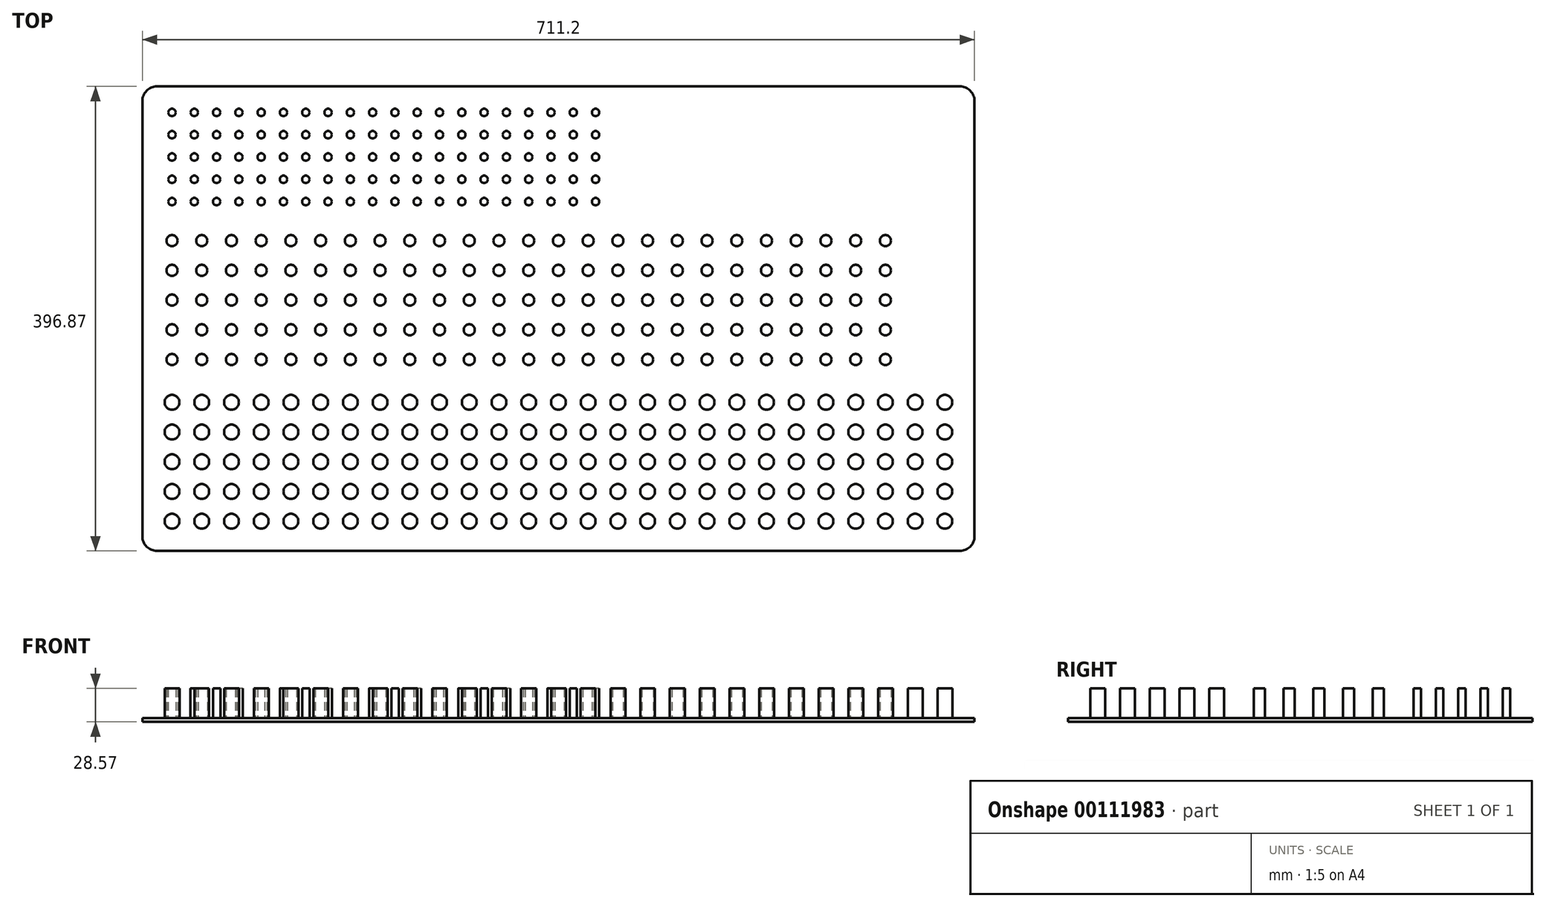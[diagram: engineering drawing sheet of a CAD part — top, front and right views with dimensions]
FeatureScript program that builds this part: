
annotation { "Feature Type Name" : "Feature", "Feature Type Description" : "" }
export const myFeature = defineFeature(function(context is Context, id is Id, definition is map)
    precondition{}
    {
        {
            var Q0;
            Q0=qCreatedBy(makeId("Top.planeOp"),FACE);
            var sketch = newSketch(context, id + "F0", { "sketchPlane" : qUnion([Q0])});
            skCircle(sketch, "E0", {"center": v(0, 97.83) * mm, "radius": 3.17 * mm});
            skCircle(sketch, "E1.0.1.0", {"center": v(0, 116.88) * mm, "radius": 3.17 * mm});
            skCircle(sketch, "E1.0.2.0", {"center": v(0, 135.93) * mm, "radius": 3.17 * mm});
            skCircle(sketch, "E1.0.3.0", {"center": v(0, 154.98) * mm, "radius": 3.17 * mm});
            skCircle(sketch, "E1.0.4.0", {"center": v(0, 174.03) * mm, "radius": 3.17 * mm});
            skCircle(sketch, "E1.1.0.0", {"center": v(19.05, 97.83) * mm, "radius": 3.17 * mm});
            skCircle(sketch, "E1.1.1.0", {"center": v(19.05, 116.88) * mm, "radius": 3.17 * mm});
            skCircle(sketch, "E1.1.2.0", {"center": v(19.05, 135.93) * mm, "radius": 3.17 * mm});
            skCircle(sketch, "E1.1.3.0", {"center": v(19.05, 154.98) * mm, "radius": 3.17 * mm});
            skCircle(sketch, "E1.1.4.0", {"center": v(19.05, 174.03) * mm, "radius": 3.17 * mm});
            skCircle(sketch, "E1.2.0.0", {"center": v(38.1, 97.83) * mm, "radius": 3.17 * mm});
            skCircle(sketch, "E1.2.1.0", {"center": v(38.1, 116.88) * mm, "radius": 3.17 * mm});
            skCircle(sketch, "E1.2.2.0", {"center": v(38.1, 135.93) * mm, "radius": 3.17 * mm});
            skCircle(sketch, "E1.2.3.0", {"center": v(38.1, 154.98) * mm, "radius": 3.17 * mm});
            skCircle(sketch, "E1.2.4.0", {"center": v(38.1, 174.03) * mm, "radius": 3.17 * mm});
            skCircle(sketch, "E1.3.0.0", {"center": v(57.15, 97.83) * mm, "radius": 3.17 * mm});
            skCircle(sketch, "E1.3.1.0", {"center": v(57.15, 116.88) * mm, "radius": 3.17 * mm});
            skCircle(sketch, "E1.3.2.0", {"center": v(57.15, 135.93) * mm, "radius": 3.17 * mm});
            skCircle(sketch, "E1.3.3.0", {"center": v(57.15, 154.98) * mm, "radius": 3.17 * mm});
            skCircle(sketch, "E1.3.4.0", {"center": v(57.15, 174.03) * mm, "radius": 3.17 * mm});
            skCircle(sketch, "E1.4.0.0", {"center": v(76.2, 97.83) * mm, "radius": 3.17 * mm});
            skCircle(sketch, "E1.4.1.0", {"center": v(76.2, 116.88) * mm, "radius": 3.17 * mm});
            skCircle(sketch, "E1.4.2.0", {"center": v(76.2, 135.93) * mm, "radius": 3.17 * mm});
            skCircle(sketch, "E1.4.3.0", {"center": v(76.2, 154.98) * mm, "radius": 3.17 * mm});
            skCircle(sketch, "E1.4.4.0", {"center": v(76.2, 174.03) * mm, "radius": 3.17 * mm});
            skCircle(sketch, "E1.5.0.0", {"center": v(95.25, 97.83) * mm, "radius": 3.17 * mm});
            skCircle(sketch, "E1.5.1.0", {"center": v(95.25, 116.88) * mm, "radius": 3.17 * mm});
            skCircle(sketch, "E1.5.2.0", {"center": v(95.25, 135.93) * mm, "radius": 3.17 * mm});
            skCircle(sketch, "E1.5.3.0", {"center": v(95.25, 154.98) * mm, "radius": 3.17 * mm});
            skCircle(sketch, "E1.5.4.0", {"center": v(95.25, 174.03) * mm, "radius": 3.17 * mm});
            skCircle(sketch, "E1.6.0.0", {"center": v(114.3, 97.83) * mm, "radius": 3.17 * mm});
            skCircle(sketch, "E1.6.1.0", {"center": v(114.3, 116.88) * mm, "radius": 3.17 * mm});
            skCircle(sketch, "E1.6.2.0", {"center": v(114.3, 135.93) * mm, "radius": 3.17 * mm});
            skCircle(sketch, "E1.6.3.0", {"center": v(114.3, 154.98) * mm, "radius": 3.17 * mm});
            skCircle(sketch, "E1.6.4.0", {"center": v(114.3, 174.03) * mm, "radius": 3.17 * mm});
            skCircle(sketch, "E1.7.0.0", {"center": v(133.35, 97.83) * mm, "radius": 3.17 * mm});
            skCircle(sketch, "E1.7.1.0", {"center": v(133.35, 116.88) * mm, "radius": 3.17 * mm});
            skCircle(sketch, "E1.7.2.0", {"center": v(133.35, 135.93) * mm, "radius": 3.17 * mm});
            skCircle(sketch, "E1.7.3.0", {"center": v(133.35, 154.98) * mm, "radius": 3.17 * mm});
            skCircle(sketch, "E1.7.4.0", {"center": v(133.35, 174.03) * mm, "radius": 3.17 * mm});
            skCircle(sketch, "E1.8.0.0", {"center": v(152.4, 97.83) * mm, "radius": 3.17 * mm});
            skCircle(sketch, "E1.8.1.0", {"center": v(152.4, 116.88) * mm, "radius": 3.17 * mm});
            skCircle(sketch, "E1.8.2.0", {"center": v(152.4, 135.93) * mm, "radius": 3.17 * mm});
            skCircle(sketch, "E1.8.3.0", {"center": v(152.4, 154.98) * mm, "radius": 3.17 * mm});
            skCircle(sketch, "E1.8.4.0", {"center": v(152.4, 174.03) * mm, "radius": 3.17 * mm});
            skCircle(sketch, "E1.9.0.0", {"center": v(171.45, 97.83) * mm, "radius": 3.17 * mm});
            skCircle(sketch, "E1.9.1.0", {"center": v(171.45, 116.88) * mm, "radius": 3.17 * mm});
            skCircle(sketch, "E1.9.2.0", {"center": v(171.45, 135.93) * mm, "radius": 3.17 * mm});
            skCircle(sketch, "E1.9.3.0", {"center": v(171.45, 154.98) * mm, "radius": 3.17 * mm});
            skCircle(sketch, "E1.9.4.0", {"center": v(171.45, 174.03) * mm, "radius": 3.17 * mm});
            skCircle(sketch, "E1.10.0.0", {"center": v(190.5, 97.83) * mm, "radius": 3.17 * mm});
            skCircle(sketch, "E1.10.1.0", {"center": v(190.5, 116.88) * mm, "radius": 3.17 * mm});
            skCircle(sketch, "E1.10.2.0", {"center": v(190.5, 135.93) * mm, "radius": 3.17 * mm});
            skCircle(sketch, "E1.10.3.0", {"center": v(190.5, 154.98) * mm, "radius": 3.17 * mm});
            skCircle(sketch, "E1.10.4.0", {"center": v(190.5, 174.03) * mm, "radius": 3.17 * mm});
            skCircle(sketch, "E1.11.0.0", {"center": v(209.55, 97.83) * mm, "radius": 3.17 * mm});
            skCircle(sketch, "E1.11.1.0", {"center": v(209.55, 116.88) * mm, "radius": 3.17 * mm});
            skCircle(sketch, "E1.11.2.0", {"center": v(209.55, 135.93) * mm, "radius": 3.17 * mm});
            skCircle(sketch, "E1.11.3.0", {"center": v(209.55, 154.98) * mm, "radius": 3.17 * mm});
            skCircle(sketch, "E1.11.4.0", {"center": v(209.55, 174.03) * mm, "radius": 3.17 * mm});
            skCircle(sketch, "E1.12.0.0", {"center": v(228.6, 97.83) * mm, "radius": 3.17 * mm});
            skCircle(sketch, "E1.12.1.0", {"center": v(228.6, 116.88) * mm, "radius": 3.17 * mm});
            skCircle(sketch, "E1.12.2.0", {"center": v(228.6, 135.93) * mm, "radius": 3.17 * mm});
            skCircle(sketch, "E1.12.3.0", {"center": v(228.6, 154.98) * mm, "radius": 3.17 * mm});
            skCircle(sketch, "E1.12.4.0", {"center": v(228.6, 174.03) * mm, "radius": 3.17 * mm});
            skCircle(sketch, "E1.13.0.0", {"center": v(247.65, 97.83) * mm, "radius": 3.17 * mm});
            skCircle(sketch, "E1.13.1.0", {"center": v(247.65, 116.88) * mm, "radius": 3.17 * mm});
            skCircle(sketch, "E1.13.2.0", {"center": v(247.65, 135.93) * mm, "radius": 3.17 * mm});
            skCircle(sketch, "E1.13.3.0", {"center": v(247.65, 154.98) * mm, "radius": 3.17 * mm});
            skCircle(sketch, "E1.13.4.0", {"center": v(247.65, 174.03) * mm, "radius": 3.17 * mm});
            skCircle(sketch, "E1.14.0.0", {"center": v(266.7, 97.83) * mm, "radius": 3.17 * mm});
            skCircle(sketch, "E1.14.1.0", {"center": v(266.7, 116.88) * mm, "radius": 3.17 * mm});
            skCircle(sketch, "E1.14.2.0", {"center": v(266.7, 135.93) * mm, "radius": 3.17 * mm});
            skCircle(sketch, "E1.14.3.0", {"center": v(266.7, 154.98) * mm, "radius": 3.17 * mm});
            skCircle(sketch, "E1.14.4.0", {"center": v(266.7, 174.03) * mm, "radius": 3.17 * mm});
            skLineSegment(sketch, "E1.direction1", {"start": v(0, 97.83) * mm, "end": v(19.05, 97.83) * mm, "construction": true});
            skLineSegment(sketch, "E1.direction2", {"start": v(0, 97.83) * mm, "end": v(0, 116.88) * mm, "construction": true});
            skLineSegment(sketch, "E2", {"start": v(0, 174.03) * mm, "end": v(0, -304.85) * mm, "construction": true});
            skCircle(sketch, "E3", {"center": v(0, 64.49) * mm, "radius": 4.76 * mm});
            skCircle(sketch, "E4.0.1.0", {"center": v(0, 39.09) * mm, "radius": 4.76 * mm});
            skCircle(sketch, "E4.0.2.0", {"center": v(0, 13.69) * mm, "radius": 4.76 * mm});
            skCircle(sketch, "E4.0.3.0", {"center": v(0, -11.71) * mm, "radius": 4.76 * mm});
            skCircle(sketch, "E4.0.4.0", {"center": v(0, -37.11) * mm, "radius": 4.76 * mm});
            skCircle(sketch, "E4.1.0.0", {"center": v(25.4, 64.49) * mm, "radius": 4.76 * mm});
            skCircle(sketch, "E4.1.1.0", {"center": v(25.4, 39.09) * mm, "radius": 4.76 * mm});
            skCircle(sketch, "E4.1.2.0", {"center": v(25.4, 13.69) * mm, "radius": 4.76 * mm});
            skCircle(sketch, "E4.1.3.0", {"center": v(25.4, -11.71) * mm, "radius": 4.76 * mm});
            skCircle(sketch, "E4.1.4.0", {"center": v(25.4, -37.11) * mm, "radius": 4.76 * mm});
            skCircle(sketch, "E4.2.0.0", {"center": v(50.8, 64.49) * mm, "radius": 4.76 * mm});
            skCircle(sketch, "E4.2.1.0", {"center": v(50.8, 39.09) * mm, "radius": 4.76 * mm});
            skCircle(sketch, "E4.2.2.0", {"center": v(50.8, 13.69) * mm, "radius": 4.76 * mm});
            skCircle(sketch, "E4.2.3.0", {"center": v(50.8, -11.71) * mm, "radius": 4.76 * mm});
            skCircle(sketch, "E4.2.4.0", {"center": v(50.8, -37.11) * mm, "radius": 4.76 * mm});
            skCircle(sketch, "E4.3.0.0", {"center": v(76.2, 64.49) * mm, "radius": 4.76 * mm});
            skCircle(sketch, "E4.3.1.0", {"center": v(76.2, 39.09) * mm, "radius": 4.76 * mm});
            skCircle(sketch, "E4.3.2.0", {"center": v(76.2, 13.69) * mm, "radius": 4.76 * mm});
            skCircle(sketch, "E4.3.3.0", {"center": v(76.2, -11.71) * mm, "radius": 4.76 * mm});
            skCircle(sketch, "E4.3.4.0", {"center": v(76.2, -37.11) * mm, "radius": 4.76 * mm});
            skCircle(sketch, "E4.4.0.0", {"center": v(101.6, 64.49) * mm, "radius": 4.76 * mm});
            skCircle(sketch, "E4.4.1.0", {"center": v(101.6, 39.09) * mm, "radius": 4.76 * mm});
            skCircle(sketch, "E4.4.2.0", {"center": v(101.6, 13.69) * mm, "radius": 4.76 * mm});
            skCircle(sketch, "E4.4.3.0", {"center": v(101.6, -11.71) * mm, "radius": 4.76 * mm});
            skCircle(sketch, "E4.4.4.0", {"center": v(101.6, -37.11) * mm, "radius": 4.76 * mm});
            skCircle(sketch, "E4.5.0.0", {"center": v(127, 64.49) * mm, "radius": 4.76 * mm});
            skCircle(sketch, "E4.5.1.0", {"center": v(127, 39.09) * mm, "radius": 4.76 * mm});
            skCircle(sketch, "E4.5.2.0", {"center": v(127, 13.69) * mm, "radius": 4.76 * mm});
            skCircle(sketch, "E4.5.3.0", {"center": v(127, -11.71) * mm, "radius": 4.76 * mm});
            skCircle(sketch, "E4.5.4.0", {"center": v(127, -37.11) * mm, "radius": 4.76 * mm});
            skCircle(sketch, "E4.6.0.0", {"center": v(152.4, 64.49) * mm, "radius": 4.76 * mm});
            skCircle(sketch, "E4.6.1.0", {"center": v(152.4, 39.09) * mm, "radius": 4.76 * mm});
            skCircle(sketch, "E4.6.2.0", {"center": v(152.4, 13.69) * mm, "radius": 4.76 * mm});
            skCircle(sketch, "E4.6.3.0", {"center": v(152.4, -11.71) * mm, "radius": 4.76 * mm});
            skCircle(sketch, "E4.6.4.0", {"center": v(152.4, -37.11) * mm, "radius": 4.76 * mm});
            skCircle(sketch, "E4.7.0.0", {"center": v(177.8, 64.49) * mm, "radius": 4.76 * mm});
            skCircle(sketch, "E4.7.1.0", {"center": v(177.8, 39.09) * mm, "radius": 4.76 * mm});
            skCircle(sketch, "E4.7.2.0", {"center": v(177.8, 13.69) * mm, "radius": 4.76 * mm});
            skCircle(sketch, "E4.7.3.0", {"center": v(177.8, -11.71) * mm, "radius": 4.76 * mm});
            skCircle(sketch, "E4.7.4.0", {"center": v(177.8, -37.11) * mm, "radius": 4.76 * mm});
            skCircle(sketch, "E4.8.0.0", {"center": v(203.2, 64.49) * mm, "radius": 4.76 * mm});
            skCircle(sketch, "E4.8.1.0", {"center": v(203.2, 39.09) * mm, "radius": 4.76 * mm});
            skCircle(sketch, "E4.8.2.0", {"center": v(203.2, 13.69) * mm, "radius": 4.76 * mm});
            skCircle(sketch, "E4.8.3.0", {"center": v(203.2, -11.71) * mm, "radius": 4.76 * mm});
            skCircle(sketch, "E4.8.4.0", {"center": v(203.2, -37.11) * mm, "radius": 4.76 * mm});
            skCircle(sketch, "E4.9.0.0", {"center": v(228.6, 64.49) * mm, "radius": 4.76 * mm});
            skCircle(sketch, "E4.9.1.0", {"center": v(228.6, 39.09) * mm, "radius": 4.76 * mm});
            skCircle(sketch, "E4.9.2.0", {"center": v(228.6, 13.69) * mm, "radius": 4.76 * mm});
            skCircle(sketch, "E4.9.3.0", {"center": v(228.6, -11.71) * mm, "radius": 4.76 * mm});
            skCircle(sketch, "E4.9.4.0", {"center": v(228.6, -37.11) * mm, "radius": 4.76 * mm});
            skCircle(sketch, "E4.10.0.0", {"center": v(254, 64.49) * mm, "radius": 4.76 * mm});
            skCircle(sketch, "E4.10.1.0", {"center": v(254, 39.09) * mm, "radius": 4.76 * mm});
            skCircle(sketch, "E4.10.2.0", {"center": v(254, 13.69) * mm, "radius": 4.76 * mm});
            skCircle(sketch, "E4.10.3.0", {"center": v(254, -11.71) * mm, "radius": 4.76 * mm});
            skCircle(sketch, "E4.10.4.0", {"center": v(254, -37.11) * mm, "radius": 4.76 * mm});
            skCircle(sketch, "E4.11.0.0", {"center": v(279.4, 64.49) * mm, "radius": 4.76 * mm});
            skCircle(sketch, "E4.11.1.0", {"center": v(279.4, 39.09) * mm, "radius": 4.76 * mm});
            skCircle(sketch, "E4.11.2.0", {"center": v(279.4, 13.69) * mm, "radius": 4.76 * mm});
            skCircle(sketch, "E4.11.3.0", {"center": v(279.4, -11.71) * mm, "radius": 4.76 * mm});
            skCircle(sketch, "E4.11.4.0", {"center": v(279.4, -37.11) * mm, "radius": 4.76 * mm});
            skCircle(sketch, "E4.12.0.0", {"center": v(304.8, 64.49) * mm, "radius": 4.76 * mm});
            skCircle(sketch, "E4.12.1.0", {"center": v(304.8, 39.09) * mm, "radius": 4.76 * mm});
            skCircle(sketch, "E4.12.2.0", {"center": v(304.8, 13.69) * mm, "radius": 4.76 * mm});
            skCircle(sketch, "E4.12.3.0", {"center": v(304.8, -11.71) * mm, "radius": 4.76 * mm});
            skCircle(sketch, "E4.12.4.0", {"center": v(304.8, -37.11) * mm, "radius": 4.76 * mm});
            skCircle(sketch, "E4.13.0.0", {"center": v(330.2, 64.49) * mm, "radius": 4.76 * mm});
            skCircle(sketch, "E4.13.1.0", {"center": v(330.2, 39.09) * mm, "radius": 4.76 * mm});
            skCircle(sketch, "E4.13.2.0", {"center": v(330.2, 13.69) * mm, "radius": 4.76 * mm});
            skCircle(sketch, "E4.13.3.0", {"center": v(330.2, -11.71) * mm, "radius": 4.76 * mm});
            skCircle(sketch, "E4.13.4.0", {"center": v(330.2, -37.11) * mm, "radius": 4.76 * mm});
            skCircle(sketch, "E4.14.0.0", {"center": v(355.6, 64.49) * mm, "radius": 4.76 * mm});
            skCircle(sketch, "E4.14.1.0", {"center": v(355.6, 39.09) * mm, "radius": 4.76 * mm});
            skCircle(sketch, "E4.14.2.0", {"center": v(355.6, 13.69) * mm, "radius": 4.76 * mm});
            skCircle(sketch, "E4.14.3.0", {"center": v(355.6, -11.71) * mm, "radius": 4.76 * mm});
            skCircle(sketch, "E4.14.4.0", {"center": v(355.6, -37.11) * mm, "radius": 4.76 * mm});
            skCircle(sketch, "E4.15.0.0", {"center": v(381, 64.49) * mm, "radius": 4.76 * mm});
            skCircle(sketch, "E4.15.1.0", {"center": v(381, 39.09) * mm, "radius": 4.76 * mm});
            skCircle(sketch, "E4.15.2.0", {"center": v(381, 13.69) * mm, "radius": 4.76 * mm});
            skCircle(sketch, "E4.15.3.0", {"center": v(381, -11.71) * mm, "radius": 4.76 * mm});
            skCircle(sketch, "E4.15.4.0", {"center": v(381, -37.11) * mm, "radius": 4.76 * mm});
            skCircle(sketch, "E4.16.0.0", {"center": v(406.4, 64.49) * mm, "radius": 4.76 * mm});
            skCircle(sketch, "E4.16.1.0", {"center": v(406.4, 39.09) * mm, "radius": 4.76 * mm});
            skCircle(sketch, "E4.16.2.0", {"center": v(406.4, 13.69) * mm, "radius": 4.76 * mm});
            skCircle(sketch, "E4.16.3.0", {"center": v(406.4, -11.71) * mm, "radius": 4.76 * mm});
            skCircle(sketch, "E4.16.4.0", {"center": v(406.4, -37.11) * mm, "radius": 4.76 * mm});
            skLineSegment(sketch, "E4.direction1", {"start": v(0, 64.49) * mm, "end": v(25.4, 64.49) * mm, "construction": true});
            skLineSegment(sketch, "E4.direction2", {"start": v(0, 64.49) * mm, "end": v(0, 39.09) * mm, "construction": true});
            skCircle(sketch, "E5", {"center": v(0, -73.62) * mm, "radius": 6.35 * mm});
            skCircle(sketch, "E6.0.15.0", {"center": v(285.75, 97.83) * mm, "radius": 3.17 * mm});
            skCircle(sketch, "E6.0.15.1", {"center": v(285.75, 116.88) * mm, "radius": 3.17 * mm});
            skCircle(sketch, "E6.0.15.2", {"center": v(285.75, 135.93) * mm, "radius": 3.17 * mm});
            skCircle(sketch, "E6.0.15.3", {"center": v(285.75, 154.98) * mm, "radius": 3.17 * mm});
            skCircle(sketch, "E6.0.15.4", {"center": v(285.75, 174.03) * mm, "radius": 3.17 * mm});
            skCircle(sketch, "E6.0.16.0", {"center": v(304.8, 97.83) * mm, "radius": 3.17 * mm});
            skCircle(sketch, "E6.0.16.1", {"center": v(304.8, 116.88) * mm, "radius": 3.17 * mm});
            skCircle(sketch, "E6.0.16.2", {"center": v(304.8, 135.93) * mm, "radius": 3.17 * mm});
            skCircle(sketch, "E6.0.16.3", {"center": v(304.8, 154.98) * mm, "radius": 3.17 * mm});
            skCircle(sketch, "E6.0.16.4", {"center": v(304.8, 174.03) * mm, "radius": 3.17 * mm});
            skCircle(sketch, "E6.0.17.0", {"center": v(323.85, 97.83) * mm, "radius": 3.17 * mm});
            skCircle(sketch, "E6.0.17.1", {"center": v(323.85, 116.88) * mm, "radius": 3.17 * mm});
            skCircle(sketch, "E6.0.17.2", {"center": v(323.85, 135.93) * mm, "radius": 3.17 * mm});
            skCircle(sketch, "E6.0.17.3", {"center": v(323.85, 154.98) * mm, "radius": 3.17 * mm});
            skCircle(sketch, "E6.0.17.4", {"center": v(323.85, 174.03) * mm, "radius": 3.17 * mm});
            skCircle(sketch, "E6.0.18.0", {"center": v(342.9, 97.83) * mm, "radius": 3.17 * mm});
            skCircle(sketch, "E6.0.18.1", {"center": v(342.9, 116.88) * mm, "radius": 3.17 * mm});
            skCircle(sketch, "E6.0.18.2", {"center": v(342.9, 135.93) * mm, "radius": 3.17 * mm});
            skCircle(sketch, "E6.0.18.3", {"center": v(342.9, 154.98) * mm, "radius": 3.17 * mm});
            skCircle(sketch, "E6.0.18.4", {"center": v(342.9, 174.03) * mm, "radius": 3.17 * mm});
            skCircle(sketch, "E6.0.19.0", {"center": v(361.95, 97.83) * mm, "radius": 3.17 * mm});
            skCircle(sketch, "E6.0.19.1", {"center": v(361.95, 116.88) * mm, "radius": 3.17 * mm});
            skCircle(sketch, "E6.0.19.2", {"center": v(361.95, 135.93) * mm, "radius": 3.17 * mm});
            skCircle(sketch, "E6.0.19.3", {"center": v(361.95, 154.98) * mm, "radius": 3.17 * mm});
            skCircle(sketch, "E6.0.19.4", {"center": v(361.95, 174.03) * mm, "radius": 3.17 * mm});
            skCircle(sketch, "E7.0.17.0", {"center": v(431.8, 64.49) * mm, "radius": 4.76 * mm});
            skCircle(sketch, "E7.0.17.1", {"center": v(431.8, 39.09) * mm, "radius": 4.76 * mm});
            skCircle(sketch, "E7.0.17.2", {"center": v(431.8, 13.69) * mm, "radius": 4.76 * mm});
            skCircle(sketch, "E7.0.17.3", {"center": v(431.8, -11.71) * mm, "radius": 4.76 * mm});
            skCircle(sketch, "E7.0.17.4", {"center": v(431.8, -37.11) * mm, "radius": 4.76 * mm});
            skCircle(sketch, "E7.0.18.0", {"center": v(457.2, 64.49) * mm, "radius": 4.76 * mm});
            skCircle(sketch, "E7.0.18.1", {"center": v(457.2, 39.09) * mm, "radius": 4.76 * mm});
            skCircle(sketch, "E7.0.18.2", {"center": v(457.2, 13.69) * mm, "radius": 4.76 * mm});
            skCircle(sketch, "E7.0.18.3", {"center": v(457.2, -11.71) * mm, "radius": 4.76 * mm});
            skCircle(sketch, "E7.0.18.4", {"center": v(457.2, -37.11) * mm, "radius": 4.76 * mm});
            skCircle(sketch, "E7.0.19.0", {"center": v(482.6, 64.49) * mm, "radius": 4.76 * mm});
            skCircle(sketch, "E7.0.19.1", {"center": v(482.6, 39.09) * mm, "radius": 4.76 * mm});
            skCircle(sketch, "E7.0.19.2", {"center": v(482.6, 13.69) * mm, "radius": 4.76 * mm});
            skCircle(sketch, "E7.0.19.3", {"center": v(482.6, -11.71) * mm, "radius": 4.76 * mm});
            skCircle(sketch, "E7.0.19.4", {"center": v(482.6, -37.11) * mm, "radius": 4.76 * mm});
            skCircle(sketch, "E7.0.20.0", {"center": v(508, 64.49) * mm, "radius": 4.76 * mm});
            skCircle(sketch, "E7.0.20.1", {"center": v(508, 39.09) * mm, "radius": 4.76 * mm});
            skCircle(sketch, "E7.0.20.2", {"center": v(508, 13.69) * mm, "radius": 4.76 * mm});
            skCircle(sketch, "E7.0.20.3", {"center": v(508, -11.71) * mm, "radius": 4.76 * mm});
            skCircle(sketch, "E7.0.20.4", {"center": v(508, -37.11) * mm, "radius": 4.76 * mm});
            skCircle(sketch, "E7.0.21.0", {"center": v(533.4, 64.49) * mm, "radius": 4.76 * mm});
            skCircle(sketch, "E7.0.21.1", {"center": v(533.4, 39.09) * mm, "radius": 4.76 * mm});
            skCircle(sketch, "E7.0.21.2", {"center": v(533.4, 13.69) * mm, "radius": 4.76 * mm});
            skCircle(sketch, "E7.0.21.3", {"center": v(533.4, -11.71) * mm, "radius": 4.76 * mm});
            skCircle(sketch, "E7.0.21.4", {"center": v(533.4, -37.11) * mm, "radius": 4.76 * mm});
            skCircle(sketch, "E7.0.22.0", {"center": v(558.8, 64.49) * mm, "radius": 4.76 * mm});
            skCircle(sketch, "E7.0.22.1", {"center": v(558.8, 39.09) * mm, "radius": 4.76 * mm});
            skCircle(sketch, "E7.0.22.2", {"center": v(558.8, 13.69) * mm, "radius": 4.76 * mm});
            skCircle(sketch, "E7.0.22.3", {"center": v(558.8, -11.71) * mm, "radius": 4.76 * mm});
            skCircle(sketch, "E7.0.22.4", {"center": v(558.8, -37.11) * mm, "radius": 4.76 * mm});
            skCircle(sketch, "E7.0.23.0", {"center": v(584.2, 64.49) * mm, "radius": 4.76 * mm});
            skCircle(sketch, "E7.0.23.1", {"center": v(584.2, 39.09) * mm, "radius": 4.76 * mm});
            skCircle(sketch, "E7.0.23.2", {"center": v(584.2, 13.69) * mm, "radius": 4.76 * mm});
            skCircle(sketch, "E7.0.23.3", {"center": v(584.2, -11.71) * mm, "radius": 4.76 * mm});
            skCircle(sketch, "E7.0.23.4", {"center": v(584.2, -37.11) * mm, "radius": 4.76 * mm});
            skCircle(sketch, "E7.0.24.0", {"center": v(609.6, 64.49) * mm, "radius": 4.76 * mm});
            skCircle(sketch, "E7.0.24.1", {"center": v(609.6, 39.09) * mm, "radius": 4.76 * mm});
            skCircle(sketch, "E7.0.24.2", {"center": v(609.6, 13.69) * mm, "radius": 4.76 * mm});
            skCircle(sketch, "E7.0.24.3", {"center": v(609.6, -11.71) * mm, "radius": 4.76 * mm});
            skCircle(sketch, "E7.0.24.4", {"center": v(609.6, -37.11) * mm, "radius": 4.76 * mm});
            skCircle(sketch, "E8.0.1.0", {"center": v(0, -99.02) * mm, "radius": 6.35 * mm});
            skCircle(sketch, "E8.0.2.0", {"center": v(0, -124.42) * mm, "radius": 6.35 * mm});
            skCircle(sketch, "E8.0.3.0", {"center": v(0, -149.82) * mm, "radius": 6.35 * mm});
            skCircle(sketch, "E8.0.4.0", {"center": v(0, -175.22) * mm, "radius": 6.35 * mm});
            skCircle(sketch, "E8.1.0.0", {"center": v(25.4, -73.62) * mm, "radius": 6.35 * mm});
            skCircle(sketch, "E8.1.1.0", {"center": v(25.4, -99.02) * mm, "radius": 6.35 * mm});
            skCircle(sketch, "E8.1.2.0", {"center": v(25.4, -124.42) * mm, "radius": 6.35 * mm});
            skCircle(sketch, "E8.1.3.0", {"center": v(25.4, -149.82) * mm, "radius": 6.35 * mm});
            skCircle(sketch, "E8.1.4.0", {"center": v(25.4, -175.22) * mm, "radius": 6.35 * mm});
            skCircle(sketch, "E8.2.0.0", {"center": v(50.8, -73.62) * mm, "radius": 6.35 * mm});
            skCircle(sketch, "E8.2.1.0", {"center": v(50.8, -99.02) * mm, "radius": 6.35 * mm});
            skCircle(sketch, "E8.2.2.0", {"center": v(50.8, -124.42) * mm, "radius": 6.35 * mm});
            skCircle(sketch, "E8.2.3.0", {"center": v(50.8, -149.82) * mm, "radius": 6.35 * mm});
            skCircle(sketch, "E8.2.4.0", {"center": v(50.8, -175.22) * mm, "radius": 6.35 * mm});
            skCircle(sketch, "E8.3.0.0", {"center": v(76.2, -73.62) * mm, "radius": 6.35 * mm});
            skCircle(sketch, "E8.3.1.0", {"center": v(76.2, -99.02) * mm, "radius": 6.35 * mm});
            skCircle(sketch, "E8.3.2.0", {"center": v(76.2, -124.42) * mm, "radius": 6.35 * mm});
            skCircle(sketch, "E8.3.3.0", {"center": v(76.2, -149.82) * mm, "radius": 6.35 * mm});
            skCircle(sketch, "E8.3.4.0", {"center": v(76.2, -175.22) * mm, "radius": 6.35 * mm});
            skCircle(sketch, "E8.4.0.0", {"center": v(101.6, -73.62) * mm, "radius": 6.35 * mm});
            skCircle(sketch, "E8.4.1.0", {"center": v(101.6, -99.02) * mm, "radius": 6.35 * mm});
            skCircle(sketch, "E8.4.2.0", {"center": v(101.6, -124.42) * mm, "radius": 6.35 * mm});
            skCircle(sketch, "E8.4.3.0", {"center": v(101.6, -149.82) * mm, "radius": 6.35 * mm});
            skCircle(sketch, "E8.4.4.0", {"center": v(101.6, -175.22) * mm, "radius": 6.35 * mm});
            skCircle(sketch, "E8.5.0.0", {"center": v(127, -73.62) * mm, "radius": 6.35 * mm});
            skCircle(sketch, "E8.5.1.0", {"center": v(127, -99.02) * mm, "radius": 6.35 * mm});
            skCircle(sketch, "E8.5.2.0", {"center": v(127, -124.42) * mm, "radius": 6.35 * mm});
            skCircle(sketch, "E8.5.3.0", {"center": v(127, -149.82) * mm, "radius": 6.35 * mm});
            skCircle(sketch, "E8.5.4.0", {"center": v(127, -175.22) * mm, "radius": 6.35 * mm});
            skCircle(sketch, "E8.6.0.0", {"center": v(152.4, -73.62) * mm, "radius": 6.35 * mm});
            skCircle(sketch, "E8.6.1.0", {"center": v(152.4, -99.02) * mm, "radius": 6.35 * mm});
            skCircle(sketch, "E8.6.2.0", {"center": v(152.4, -124.42) * mm, "radius": 6.35 * mm});
            skCircle(sketch, "E8.6.3.0", {"center": v(152.4, -149.82) * mm, "radius": 6.35 * mm});
            skCircle(sketch, "E8.6.4.0", {"center": v(152.4, -175.22) * mm, "radius": 6.35 * mm});
            skCircle(sketch, "E8.7.0.0", {"center": v(177.8, -73.62) * mm, "radius": 6.35 * mm});
            skCircle(sketch, "E8.7.1.0", {"center": v(177.8, -99.02) * mm, "radius": 6.35 * mm});
            skCircle(sketch, "E8.7.2.0", {"center": v(177.8, -124.42) * mm, "radius": 6.35 * mm});
            skCircle(sketch, "E8.7.3.0", {"center": v(177.8, -149.82) * mm, "radius": 6.35 * mm});
            skCircle(sketch, "E8.7.4.0", {"center": v(177.8, -175.22) * mm, "radius": 6.35 * mm});
            skCircle(sketch, "E8.8.0.0", {"center": v(203.2, -73.62) * mm, "radius": 6.35 * mm});
            skCircle(sketch, "E8.8.1.0", {"center": v(203.2, -99.02) * mm, "radius": 6.35 * mm});
            skCircle(sketch, "E8.8.2.0", {"center": v(203.2, -124.42) * mm, "radius": 6.35 * mm});
            skCircle(sketch, "E8.8.3.0", {"center": v(203.2, -149.82) * mm, "radius": 6.35 * mm});
            skCircle(sketch, "E8.8.4.0", {"center": v(203.2, -175.22) * mm, "radius": 6.35 * mm});
            skCircle(sketch, "E8.9.0.0", {"center": v(228.6, -73.62) * mm, "radius": 6.35 * mm});
            skCircle(sketch, "E8.9.1.0", {"center": v(228.6, -99.02) * mm, "radius": 6.35 * mm});
            skCircle(sketch, "E8.9.2.0", {"center": v(228.6, -124.42) * mm, "radius": 6.35 * mm});
            skCircle(sketch, "E8.9.3.0", {"center": v(228.6, -149.82) * mm, "radius": 6.35 * mm});
            skCircle(sketch, "E8.9.4.0", {"center": v(228.6, -175.22) * mm, "radius": 6.35 * mm});
            skCircle(sketch, "E8.10.0.0", {"center": v(254, -73.62) * mm, "radius": 6.35 * mm});
            skCircle(sketch, "E8.10.1.0", {"center": v(254, -99.02) * mm, "radius": 6.35 * mm});
            skCircle(sketch, "E8.10.2.0", {"center": v(254, -124.42) * mm, "radius": 6.35 * mm});
            skCircle(sketch, "E8.10.3.0", {"center": v(254, -149.82) * mm, "radius": 6.35 * mm});
            skCircle(sketch, "E8.10.4.0", {"center": v(254, -175.22) * mm, "radius": 6.35 * mm});
            skCircle(sketch, "E8.11.0.0", {"center": v(279.4, -73.62) * mm, "radius": 6.35 * mm});
            skCircle(sketch, "E8.11.1.0", {"center": v(279.4, -99.02) * mm, "radius": 6.35 * mm});
            skCircle(sketch, "E8.11.2.0", {"center": v(279.4, -124.42) * mm, "radius": 6.35 * mm});
            skCircle(sketch, "E8.11.3.0", {"center": v(279.4, -149.82) * mm, "radius": 6.35 * mm});
            skCircle(sketch, "E8.11.4.0", {"center": v(279.4, -175.22) * mm, "radius": 6.35 * mm});
            skCircle(sketch, "E8.12.0.0", {"center": v(304.8, -73.62) * mm, "radius": 6.35 * mm});
            skCircle(sketch, "E8.12.1.0", {"center": v(304.8, -99.02) * mm, "radius": 6.35 * mm});
            skCircle(sketch, "E8.12.2.0", {"center": v(304.8, -124.42) * mm, "radius": 6.35 * mm});
            skCircle(sketch, "E8.12.3.0", {"center": v(304.8, -149.82) * mm, "radius": 6.35 * mm});
            skCircle(sketch, "E8.12.4.0", {"center": v(304.8, -175.22) * mm, "radius": 6.35 * mm});
            skCircle(sketch, "E8.13.0.0", {"center": v(330.2, -73.62) * mm, "radius": 6.35 * mm});
            skCircle(sketch, "E8.13.1.0", {"center": v(330.2, -99.02) * mm, "radius": 6.35 * mm});
            skCircle(sketch, "E8.13.2.0", {"center": v(330.2, -124.42) * mm, "radius": 6.35 * mm});
            skCircle(sketch, "E8.13.3.0", {"center": v(330.2, -149.82) * mm, "radius": 6.35 * mm});
            skCircle(sketch, "E8.13.4.0", {"center": v(330.2, -175.22) * mm, "radius": 6.35 * mm});
            skCircle(sketch, "E8.14.0.0", {"center": v(355.6, -73.62) * mm, "radius": 6.35 * mm});
            skCircle(sketch, "E8.14.1.0", {"center": v(355.6, -99.02) * mm, "radius": 6.35 * mm});
            skCircle(sketch, "E8.14.2.0", {"center": v(355.6, -124.42) * mm, "radius": 6.35 * mm});
            skCircle(sketch, "E8.14.3.0", {"center": v(355.6, -149.82) * mm, "radius": 6.35 * mm});
            skCircle(sketch, "E8.14.4.0", {"center": v(355.6, -175.22) * mm, "radius": 6.35 * mm});
            skCircle(sketch, "E8.15.0.0", {"center": v(381, -73.62) * mm, "radius": 6.35 * mm});
            skCircle(sketch, "E8.15.1.0", {"center": v(381, -99.02) * mm, "radius": 6.35 * mm});
            skCircle(sketch, "E8.15.2.0", {"center": v(381, -124.42) * mm, "radius": 6.35 * mm});
            skCircle(sketch, "E8.15.3.0", {"center": v(381, -149.82) * mm, "radius": 6.35 * mm});
            skCircle(sketch, "E8.15.4.0", {"center": v(381, -175.22) * mm, "radius": 6.35 * mm});
            skCircle(sketch, "E8.16.0.0", {"center": v(406.4, -73.62) * mm, "radius": 6.35 * mm});
            skCircle(sketch, "E8.16.1.0", {"center": v(406.4, -99.02) * mm, "radius": 6.35 * mm});
            skCircle(sketch, "E8.16.2.0", {"center": v(406.4, -124.42) * mm, "radius": 6.35 * mm});
            skCircle(sketch, "E8.16.3.0", {"center": v(406.4, -149.82) * mm, "radius": 6.35 * mm});
            skCircle(sketch, "E8.16.4.0", {"center": v(406.4, -175.22) * mm, "radius": 6.35 * mm});
            skCircle(sketch, "E8.17.0.0", {"center": v(431.8, -73.62) * mm, "radius": 6.35 * mm});
            skCircle(sketch, "E8.17.1.0", {"center": v(431.8, -99.02) * mm, "radius": 6.35 * mm});
            skCircle(sketch, "E8.17.2.0", {"center": v(431.8, -124.42) * mm, "radius": 6.35 * mm});
            skCircle(sketch, "E8.17.3.0", {"center": v(431.8, -149.82) * mm, "radius": 6.35 * mm});
            skCircle(sketch, "E8.17.4.0", {"center": v(431.8, -175.22) * mm, "radius": 6.35 * mm});
            skCircle(sketch, "E8.18.0.0", {"center": v(457.2, -73.62) * mm, "radius": 6.35 * mm});
            skCircle(sketch, "E8.18.1.0", {"center": v(457.2, -99.02) * mm, "radius": 6.35 * mm});
            skCircle(sketch, "E8.18.2.0", {"center": v(457.2, -124.42) * mm, "radius": 6.35 * mm});
            skCircle(sketch, "E8.18.3.0", {"center": v(457.2, -149.82) * mm, "radius": 6.35 * mm});
            skCircle(sketch, "E8.18.4.0", {"center": v(457.2, -175.22) * mm, "radius": 6.35 * mm});
            skCircle(sketch, "E8.19.0.0", {"center": v(482.6, -73.62) * mm, "radius": 6.35 * mm});
            skCircle(sketch, "E8.19.1.0", {"center": v(482.6, -99.02) * mm, "radius": 6.35 * mm});
            skCircle(sketch, "E8.19.2.0", {"center": v(482.6, -124.42) * mm, "radius": 6.35 * mm});
            skCircle(sketch, "E8.19.3.0", {"center": v(482.6, -149.82) * mm, "radius": 6.35 * mm});
            skCircle(sketch, "E8.19.4.0", {"center": v(482.6, -175.22) * mm, "radius": 6.35 * mm});
            skCircle(sketch, "E8.20.0.0", {"center": v(508, -73.62) * mm, "radius": 6.35 * mm});
            skCircle(sketch, "E8.20.1.0", {"center": v(508, -99.02) * mm, "radius": 6.35 * mm});
            skCircle(sketch, "E8.20.2.0", {"center": v(508, -124.42) * mm, "radius": 6.35 * mm});
            skCircle(sketch, "E8.20.3.0", {"center": v(508, -149.82) * mm, "radius": 6.35 * mm});
            skCircle(sketch, "E8.20.4.0", {"center": v(508, -175.22) * mm, "radius": 6.35 * mm});
            skCircle(sketch, "E8.21.0.0", {"center": v(533.4, -73.62) * mm, "radius": 6.35 * mm});
            skCircle(sketch, "E8.21.1.0", {"center": v(533.4, -99.02) * mm, "radius": 6.35 * mm});
            skCircle(sketch, "E8.21.2.0", {"center": v(533.4, -124.42) * mm, "radius": 6.35 * mm});
            skCircle(sketch, "E8.21.3.0", {"center": v(533.4, -149.82) * mm, "radius": 6.35 * mm});
            skCircle(sketch, "E8.21.4.0", {"center": v(533.4, -175.22) * mm, "radius": 6.35 * mm});
            skCircle(sketch, "E8.22.0.0", {"center": v(558.8, -73.62) * mm, "radius": 6.35 * mm});
            skCircle(sketch, "E8.22.1.0", {"center": v(558.8, -99.02) * mm, "radius": 6.35 * mm});
            skCircle(sketch, "E8.22.2.0", {"center": v(558.8, -124.42) * mm, "radius": 6.35 * mm});
            skCircle(sketch, "E8.22.3.0", {"center": v(558.8, -149.82) * mm, "radius": 6.35 * mm});
            skCircle(sketch, "E8.22.4.0", {"center": v(558.8, -175.22) * mm, "radius": 6.35 * mm});
            skCircle(sketch, "E8.23.0.0", {"center": v(584.2, -73.62) * mm, "radius": 6.35 * mm});
            skCircle(sketch, "E8.23.1.0", {"center": v(584.2, -99.02) * mm, "radius": 6.35 * mm});
            skCircle(sketch, "E8.23.2.0", {"center": v(584.2, -124.42) * mm, "radius": 6.35 * mm});
            skCircle(sketch, "E8.23.3.0", {"center": v(584.2, -149.82) * mm, "radius": 6.35 * mm});
            skCircle(sketch, "E8.23.4.0", {"center": v(584.2, -175.22) * mm, "radius": 6.35 * mm});
            skCircle(sketch, "E8.24.0.0", {"center": v(609.6, -73.62) * mm, "radius": 6.35 * mm});
            skCircle(sketch, "E8.24.1.0", {"center": v(609.6, -99.02) * mm, "radius": 6.35 * mm});
            skCircle(sketch, "E8.24.2.0", {"center": v(609.6, -124.42) * mm, "radius": 6.35 * mm});
            skCircle(sketch, "E8.24.3.0", {"center": v(609.6, -149.82) * mm, "radius": 6.35 * mm});
            skCircle(sketch, "E8.24.4.0", {"center": v(609.6, -175.22) * mm, "radius": 6.35 * mm});
            skCircle(sketch, "E8.25.0.0", {"center": v(635, -73.62) * mm, "radius": 6.35 * mm});
            skCircle(sketch, "E8.25.1.0", {"center": v(635, -99.02) * mm, "radius": 6.35 * mm});
            skCircle(sketch, "E8.25.2.0", {"center": v(635, -124.42) * mm, "radius": 6.35 * mm});
            skCircle(sketch, "E8.25.3.0", {"center": v(635, -149.82) * mm, "radius": 6.35 * mm});
            skCircle(sketch, "E8.25.4.0", {"center": v(635, -175.22) * mm, "radius": 6.35 * mm});
            skCircle(sketch, "E8.26.0.0", {"center": v(660.4, -73.62) * mm, "radius": 6.35 * mm});
            skCircle(sketch, "E8.26.1.0", {"center": v(660.4, -99.02) * mm, "radius": 6.35 * mm});
            skCircle(sketch, "E8.26.2.0", {"center": v(660.4, -124.42) * mm, "radius": 6.35 * mm});
            skCircle(sketch, "E8.26.3.0", {"center": v(660.4, -149.82) * mm, "radius": 6.35 * mm});
            skCircle(sketch, "E8.26.4.0", {"center": v(660.4, -175.22) * mm, "radius": 6.35 * mm});
            skLineSegment(sketch, "E8.direction1", {"start": v(0, -73.62) * mm, "end": v(25.4, -73.62) * mm, "construction": true});
            skLineSegment(sketch, "E8.direction2", {"start": v(0, -73.62) * mm, "end": v(0, -99.02) * mm, "construction": true});
            skSolve(sketch);
        }
        {
            var Q0;
            Q0 = qSketchRegion(id + "F0", true);
            extrude(context, id + "F1", {"entities" : qUnion([Q0]), "depth" : 25.4 * mm, "offsetDistance" : 25.4 * mm});
        }
        {
            var Q0;
            Q0=qCreatedBy(makeId("Top.planeOp"),FACE);
            var sketch = newSketch(context, id + "F2", { "sketchPlane" : qUnion([Q0])});
            skLineSegment(sketch, "E9.bottom", {"start": v(-12.7, 196.25) * mm, "end": v(673.1, 196.25) * mm});
            skLineSegment(sketch, "E9.top", {"start": v(-12.7, -200.62) * mm, "end": v(673.1, -200.62) * mm});
            skLineSegment(sketch, "E9.left", {"start": v(-25.4, 183.55) * mm, "end": v(-25.4, -187.92) * mm});
            skLineSegment(sketch, "E9.right", {"start": v(685.8, 183.55) * mm, "end": v(685.8, -187.92) * mm});
            skPoint(sketch, "E10.visualSharp", {"position": v(-25.4, 196.25) * mm});
            skArc(sketch, "E10.filletArc", {"start": v(-12.7, 196.25) * mm, "mid": v(-21.68, 192.53) * mm, "end": v(-25.4, 183.55) * mm});
            skPoint(sketch, "E11.visualSharp", {"position": v(-25.4, -200.62) * mm});
            skArc(sketch, "E11.filletArc", {"start": v(-25.4, -187.92) * mm, "mid": v(-21.68, -196.9) * mm, "end": v(-12.7, -200.62) * mm});
            skPoint(sketch, "E12.visualSharp", {"position": v(685.8, -200.62) * mm});
            skArc(sketch, "E12.filletArc", {"start": v(673.1, -200.62) * mm, "mid": v(682.08, -196.9) * mm, "end": v(685.8, -187.92) * mm});
            skPoint(sketch, "E13.visualSharp", {"position": v(685.8, 196.25) * mm});
            skArc(sketch, "E13.filletArc", {"start": v(685.8, 183.55) * mm, "mid": v(682.08, 192.53) * mm, "end": v(673.1, 196.25) * mm});
            skSolve(sketch);
        }
        {
            var Q0;
            Q0 = qSketchRegion(id + "F2", true);
            extrude(context, id + "F3", {"entities" : qUnion([Q0]), "operationType" : NewBodyOperationType.ADD, "oppositeDirection" : true, "depth" : 3.17 * mm, "offsetDistance" : 25.4 * mm});
        }
    });
